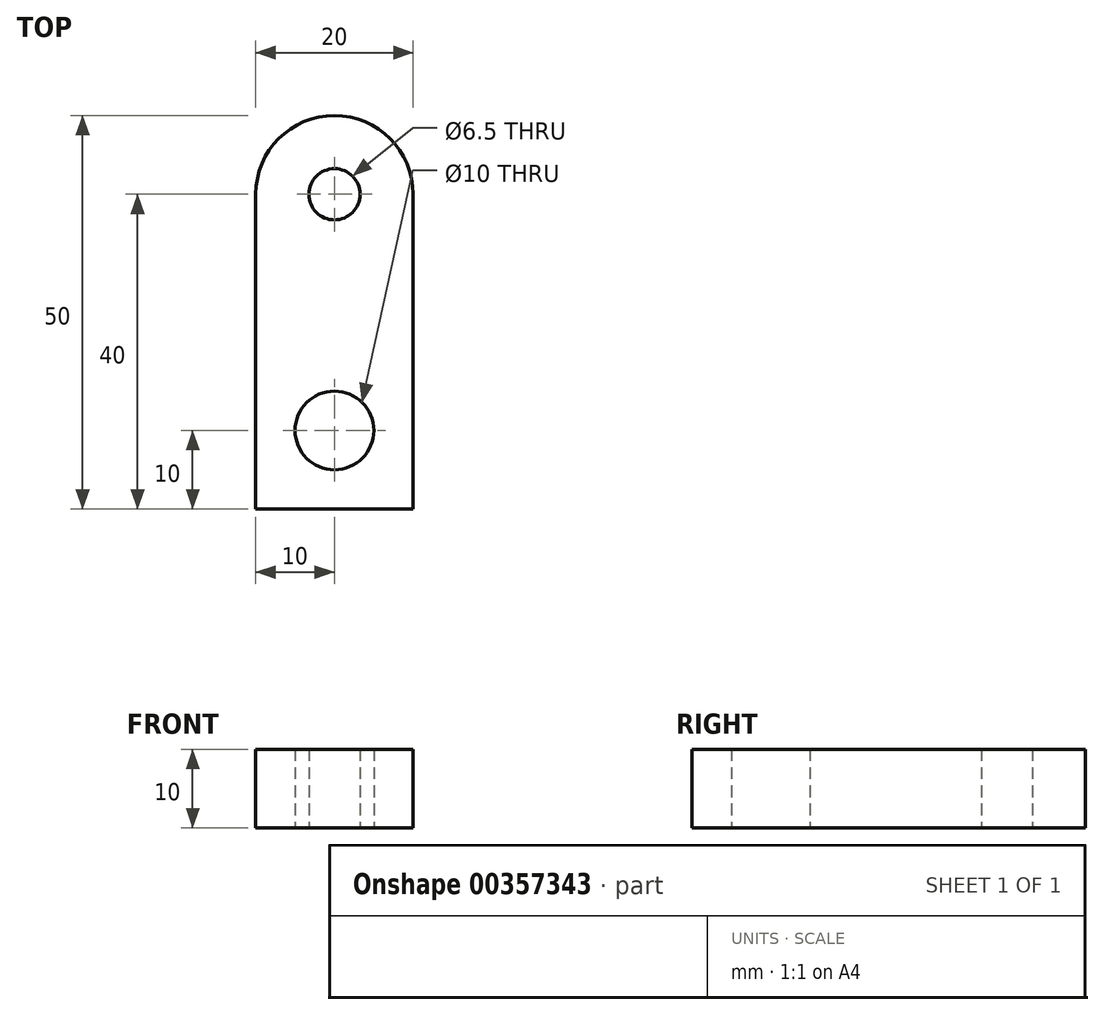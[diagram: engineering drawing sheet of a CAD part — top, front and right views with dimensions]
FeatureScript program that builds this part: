
annotation { "Feature Type Name" : "Feature", "Feature Type Description" : "" }
export const myFeature = defineFeature(function(context is Context, id is Id, definition is map)
    precondition{}
    {
        {
            var Q0;
            Q0=qCreatedBy(makeId("Top.planeOp"),FACE);
            var sketch = newSketch(context, id + "F0", { "sketchPlane" : qUnion([Q0])});
            skLineSegment(sketch, "E0.bottom", {"start": v(10, -20) * mm, "end": v(-10, -20) * mm});
            skLineSegment(sketch, "E0.top", {"start": v(10, 20) * mm, "end": v(-10, 20) * mm});
            skLineSegment(sketch, "E0.left", {"start": v(10, -20) * mm, "end": v(10, 20) * mm});
            skLineSegment(sketch, "E0.right", {"start": v(-10, -20) * mm, "end": v(-10, 20) * mm});
            skPoint(sketch, "E0.middle", {"position": v(0, 0) * mm});
            skArc(sketch, "E1", {"start": v(10, 20) * mm, "mid": v(0, 30) * mm, "end": v(-10, 20) * mm});
            skCircle(sketch, "E2", {"center": v(0, -10) * mm, "radius": 5 * mm});
            skCircle(sketch, "E3", {"center": v(0, 20) * mm, "radius": 3.25 * mm});
            skSolve(sketch);
        }
        {
            var Q0;
            {var subQ0=sQuery(id+"F0.wireOp",EDGE,"E1");Q0=makeQuery(id+"F0.imprint","IMPRINT",FACE,{"disambiguationData":[TD([[makeQuery(id+"F0.imprint","IMPRINT",EDGE,{"derivedFrom":subQ0}),1.0]])]});}
            var Q1;
            Q1=makeQuery(id+"F0.imprint","IMPRINT",FACE,{"disambiguationData":[TD([[makeQuery(id+"F0.imprint","IMPRINT",EDGE,{"derivedFrom":sQuery(id+"F0.wireOp",EDGE,"E0.bottom")}),-1.0]])]});
            extrude(context, id + "F1", {"entities" : qUnion([Q0, Q1]), "depth" : 10 * mm});
        }
    });
